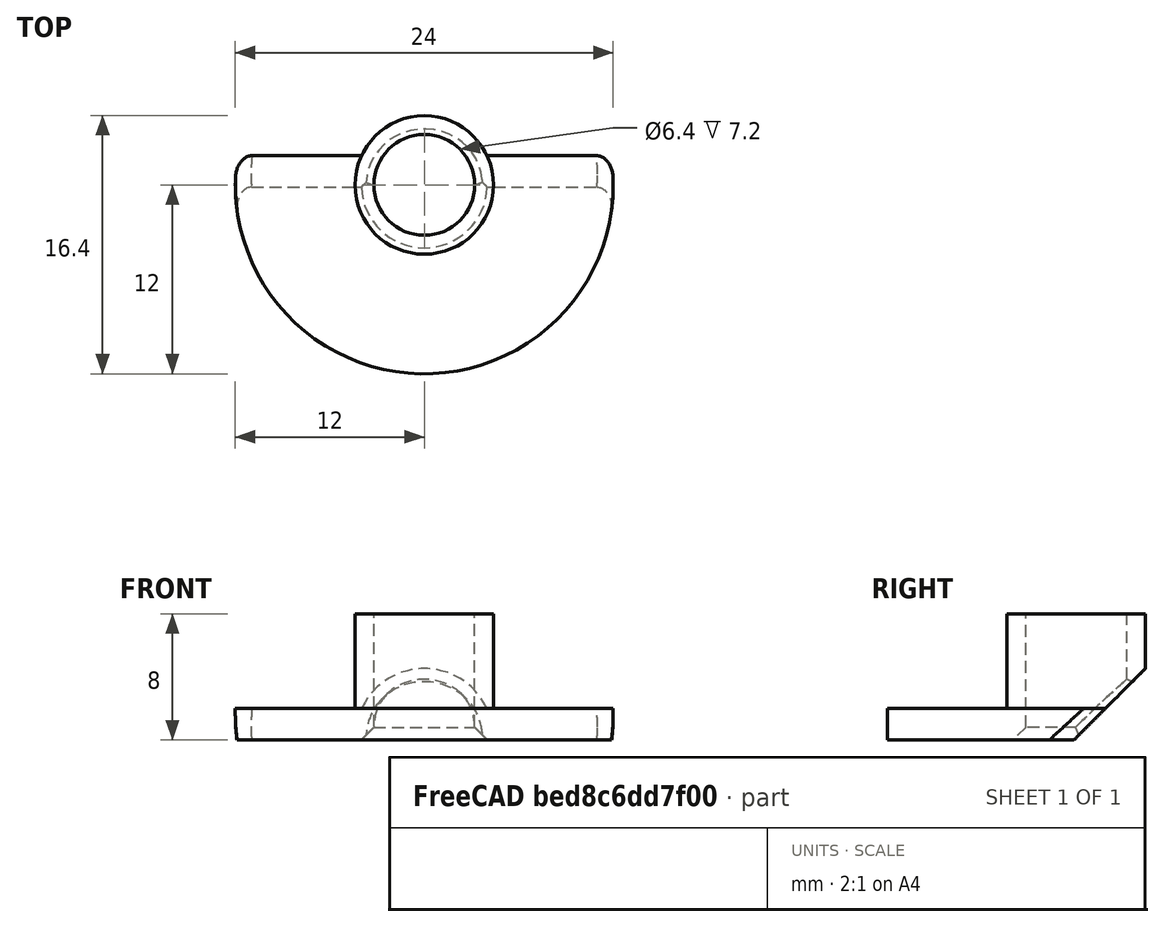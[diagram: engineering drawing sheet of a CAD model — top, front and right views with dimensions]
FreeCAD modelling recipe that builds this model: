
FCSTD DOCUMENT  (FreeCAD 0.16R)
Label: CPSpring
License: All rights reserved
LicenseURL: http://en.wikipedia.org/wiki/All_rights_reserved
objects: Part::Cylinder×3, Part::Cut×2, PartDesign::Chamfer×2, Sketcher::SketchObject×1, Part::Box×1, Part::MultiFuse×1, PartDesign::Fillet×1, Mesh::Feature×1
note: 11 computed .brp shape members not serialized (recipe doc carries the construction recipe); baked Part::Feature solids carry a one-line shape summary decoded from their .brp

FEATURE [Part::Cylinder] Cylinder  label="Spacer"
  Angle = 360
  Height = 8
  Placement = pos=(0,0,3) rot=(0,0,1;0rad)
  Radius = 4.4
FEATURE [Part::Cylinder] Cylinder001  label="SpringStop"
  Angle = 360
  Height = 2
  Placement = pos=(0,0,3) rot=(0,0,1;0rad)
  Radius = 12
FEATURE [Part::Cylinder] Cylinder003  label="hole"
  Angle = 360
  Height = 24
  Placement = pos=(0,0,-6) rot=(0,0,1;0rad)
  Radius = 3.2
FEATURE [Sketcher::SketchObject] Sketch
  Placement = pos=(0,0,4.5) rot=(0,0,1;0rad)
  sketch-geometry (1):
    g0: Circle CenterX=-9.85207 CenterY=1.7137 CenterZ=0 NormalX=0 NormalY=0 NormalZ=1 Radius=0.5
  constraints (2):
    c: Radius(g0) = 0.5
    c: Distance(g-1,g0) = 10
FEATURE [Part::Box] Box  label="Cube"
  Height = 10
  Length = 38
  Placement = pos=(-15,4,-7) rot=(1,0,0;0.785398rad)
  Width = 15
FEATURE [Part::MultiFuse] Fusion
  Shapes = -> [Cylinder,Cylinder001]
FEATURE [Part::Cut] Cut
  Base = -> Fusion
  Tool = -> Cylinder003
FEATURE [Part::Cut] Cut001
  Base = -> Cut
  Tool = -> Box
FEATURE [PartDesign::Fillet] Fillet
  Base = -> Cut001 [Edge15,Edge21]
  Radius = 1
FEATURE [PartDesign::Chamfer] Chamfer
  Base = -> Fillet [Edge24]
  Size = 0.5
FEATURE [PartDesign::Chamfer] Chamfer001
  Base = -> Chamfer [Edge15]
  Size = 0.8
FEATURE [Mesh::Feature] Mesh  label="Chamfer001 (Meshed)"
